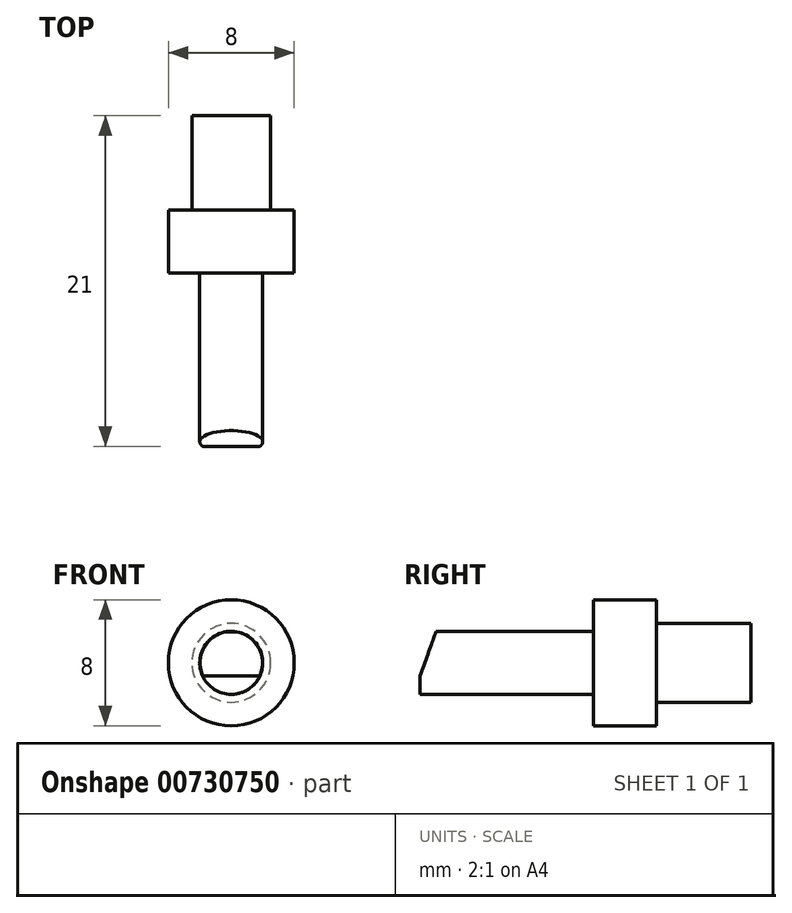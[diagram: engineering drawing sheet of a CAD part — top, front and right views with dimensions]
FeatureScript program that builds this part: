
annotation { "Feature Type Name" : "Feature", "Feature Type Description" : "" }
export const myFeature = defineFeature(function(context is Context, id is Id, definition is map)
    precondition{}
    {
        {
            var Q0;
            Q0=qCreatedBy(makeId("Front.planeOp"),FACE);
            var sketch = newSketch(context, id + "F0", { "sketchPlane" : qUnion([Q0])});
            skCircle(sketch, "E0", {"center": v(0, 0) * mm, "radius": 4 * mm});
            skSolve(sketch);
        }
        {
            var Q0;
            Q0=makeQuery(id+"F0.imprint","IMPRINT",FACE,{"disambiguationData":[TD([[makeQuery(id+"F0.imprint","IMPRINT",EDGE,{"derivedFrom":sQuery(id+"F0.wireOp",EDGE,"E0")}),1.0]])]});
            extrude(context, id + "F1", {"entities" : qUnion([Q0]), "oppositeDirection" : true, "depth" : 4 * mm, "offsetDistance" : 25 * mm});
        }
        {
            var Q0;
            Q0=makeQuery(id+"F1.opExtrude","CAP_FACE",FACE,{"disambiguationData":[OSD([sQuery(id+"F0.wireOp",EDGE,"E0")])],"isStart":true});
            var sketch = newSketch(context, id + "F2", { "sketchPlane" : qUnion([Q0])});
            skCircle(sketch, "E1", {"center": v(0, 0) * mm, "radius": 2 * mm});
            skSolve(sketch);
        }
        {
            var Q0;
            Q0=makeQuery(id+"F2.imprint","IMPRINT",FACE,{"disambiguationData":[TD([[makeQuery(id+"F2.imprint","IMPRINT",EDGE,{"derivedFrom":sQuery(id+"F2.wireOp",EDGE,"E1")}),1.0]])]});
            extrude(context, id + "F3", {"entities" : qUnion([Q0]), "operationType" : NewBodyOperationType.ADD, "depth" : 11 * mm, "offsetDistance" : 25 * mm});
        }
        {
            var Q0;
            Q0=makeQuery(id+"F1.opExtrude","CAP_FACE",FACE,{"disambiguationData":[OSD([sQuery(id+"F0.wireOp",EDGE,"E0")])],"isStart":false});
            var sketch = newSketch(context, id + "F4", { "sketchPlane" : qUnion([Q0])});
            skCircle(sketch, "E2", {"center": v(0, 0) * mm, "radius": 2.5 * mm});
            skSolve(sketch);
        }
        {
            var Q0;
            Q0=makeQuery(id+"F4.imprint","IMPRINT",FACE,{"disambiguationData":[TD([[makeQuery(id+"F4.imprint","IMPRINT",EDGE,{"derivedFrom":sQuery(id+"F4.wireOp",EDGE,"E2")}),1.0]])]});
            extrude(context, id + "F5", {"entities" : qUnion([Q0]), "operationType" : NewBodyOperationType.ADD, "depth" : 6 * mm, "offsetDistance" : 25 * mm});
        }
        {
            var Q0;
            Q0=qCreatedBy(makeId("Right.planeOp"),FACE);
            var sketch = newSketch(context, id + "F6", { "sketchPlane" : qUnion([Q0])});
            skLineSegment(sketch, "E3", {"start": v(-11, 2) * mm, "end": v(-10, 2) * mm});
            skLineSegment(sketch, "E4", {"start": v(-11, 2) * mm, "end": v(-11, -0.82) * mm});
            skLineSegment(sketch, "E5", {"start": v(-10, 2) * mm, "end": v(-11, -0.82) * mm});
            skSolve(sketch);
        }
        {
            var Q0;
            Q0=qSketchRegion(id+"F6",true);
            extrude(context, id + "F7", {"entities" : qUnion([Q0]), "operationType" : NewBodyOperationType.REMOVE, "endBound" : BoundingType.SYMMETRIC, "oppositeDirection" : true, "depth" : 4 * mm, "offsetDistance" : 25 * mm});
        }
    });
